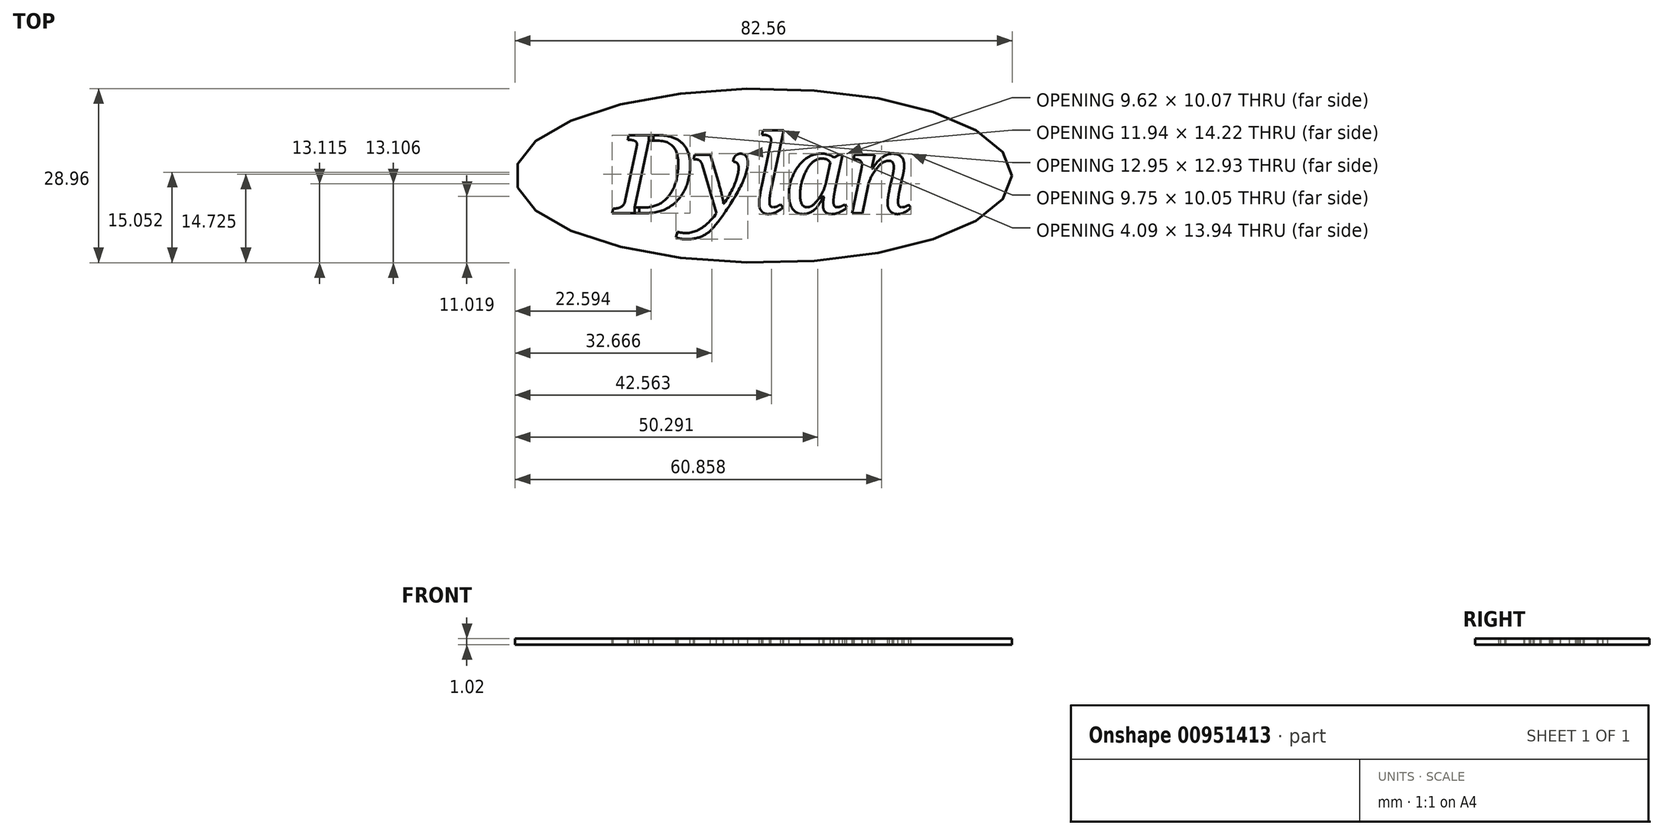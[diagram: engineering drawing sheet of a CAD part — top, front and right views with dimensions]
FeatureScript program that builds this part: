
annotation { "Feature Type Name" : "Feature", "Feature Type Description" : "" }
export const myFeature = defineFeature(function(context is Context, id is Id, definition is map)
    precondition{}
    {
        {
            var Q0;
            Q0=qCreatedBy(makeId("Top.planeOp"),FACE);
            var sketch = newSketch(context, id + "F0", { "sketchPlane" : qUnion([Q0])});
            skEllipse(sketch, "E0", {"center": v(0, 0) * mm, "majorRadius": 41.28 * mm, "minorRadius": 14.48 * mm, "majorAxis": v(1, 0)});
            skSolve(sketch);
        }
        {
            var Q0;
            Q0=makeQuery(id+"F0.imprint","IMPRINT",FACE,{"disambiguationData":[TD([[makeQuery(id+"F0.imprint","IMPRINT",EDGE,{"derivedFrom":sQuery(id+"F0.wireOp",EDGE,"E0")}),1.0]])]});
            extrude(context, id + "F1", {"entities" : qUnion([Q0]), "depth" : 1.02 * mm, "offsetDistance" : 25.4 * mm});
        }
        {
            var Q0;
            Q0=makeQuery(id+"F1.opExtrude","CAP_FACE",FACE,{"disambiguationData":[OSD([sQuery(id+"F0.wireOp",EDGE,"E0")])],"isStart":false});
            var sketch = newSketch(context, id + "F2", { "sketchPlane" : qUnion([Q0])});
            skText(sketch, "E1", { "text": "Dylan", "fontName": "NotoSerif-Italic.ttf"});
            const initialGuessF2  = {"E1": [-0.02478, -0.00622, 1, 0, 0.01304]};
            skSetInitialGuess(sketch, initialGuessF2);
            skSolve(sketch);
        }
        {
            var Q0;
            Q0 = qSketchRegion(id + "F2", true);
            extrude(context, id + "F3", {"entities" : qUnion([Q0]), "operationType" : NewBodyOperationType.REMOVE, "endBound" : BoundingType.THROUGH_ALL, "oppositeDirection" : true, "depth" : 25.4 * mm, "offsetDistance" : 25.4 * mm});
        }
        {
            var Q0;
            Q0=makeQuery(id+"F3.boolean.opBoolean","SPLIT",FACE,{"disambiguationData":[TD([makeQuery(id+"F3.opExtrude","SWEPT_FACE",FACE,{"disambiguationData":[OSD([sQuery(id+"F2.wireOp",EDGE,"E1.sketch_text.stroke-14")])]})])],"derivedFrom":makeQuery(id+"F1.opExtrude","CAP_FACE",FACE,{"disambiguationData":[OSD([sQuery(id+"F0.wireOp",EDGE,"E0")])],"isStart":false})});
            var sketch = newSketch(context, id + "F4", { "sketchPlane" : qUnion([Q0])});
            skPoint(sketch, "E2.oppositeSnap0", {"position": v(-18.34, 5.81) * mm});
            skLineSegment(sketch, "E2.bottom", {"start": v(-19.06, 5.81) * mm, "end": v(-18.34, 5.81) * mm});
            skLineSegment(sketch, "E2.top", {"start": v(-19.06, 6.74) * mm, "end": v(-18.34, 6.74) * mm});
            skLineSegment(sketch, "E2.left", {"start": v(-19.06, 5.81) * mm, "end": v(-19.06, 6.74) * mm});
            skLineSegment(sketch, "E2.right", {"start": v(-18.34, 5.81) * mm, "end": v(-18.34, 6.74) * mm});
            skPoint(sketch, "E3.oppositeSnap0", {"position": v(-20.64, -5.3) * mm});
            skLineSegment(sketch, "E3.bottom", {"start": v(-21.43, -5.3) * mm, "end": v(-20.64, -5.3) * mm});
            skLineSegment(sketch, "E3.top", {"start": v(-21.43, -6.23) * mm, "end": v(-20.64, -6.23) * mm});
            skLineSegment(sketch, "E3.left", {"start": v(-21.43, -5.3) * mm, "end": v(-21.43, -6.23) * mm});
            skLineSegment(sketch, "E3.right", {"start": v(-20.64, -5.3) * mm, "end": v(-20.64, -6.23) * mm});
            skLineSegment(sketch, "E4.bottom", {"start": v(9.94, -3.7) * mm, "end": v(9.23, -3.7) * mm});
            skLineSegment(sketch, "E4.top", {"start": v(9.94, -3.49) * mm, "end": v(9.23, -3.49) * mm});
            skLineSegment(sketch, "E4.left", {"start": v(9.94, -3.7) * mm, "end": v(9.94, -3.49) * mm});
            skLineSegment(sketch, "E4.right", {"start": v(9.23, -3.7) * mm, "end": v(9.23, -3.49) * mm});
            skSolve(sketch);
        }
        {
            var Q0;
            Q0 = qSketchRegion(id + "F4", true);
            var Q1;
            {var subQ0=sQuery(id+"F0.wireOp",EDGE,"E0");Q1=makeQuery(id+"F3.boolean.opBoolean","SPLIT",FACE,{"disambiguationData":[TD([makeQuery(id+"F1.opExtrude","SWEPT_FACE",FACE,{"disambiguationData":[OSD([subQ0])]})])],"derivedFrom":makeQuery(id+"F1.opExtrude","CAP_FACE",FACE,{"disambiguationData":[OSD([subQ0])],"isStart":true})});}
            extrude(context, id + "F5", {"entities" : qUnion([Q0]), "endBound" : BoundingType.UP_TO_SURFACE, "oppositeDirection" : true, "depth" : 25.4 * mm, "endBoundEntityFace" : qUnion([Q1]), "offsetDistance" : 25.4 * mm});
        }
    });
